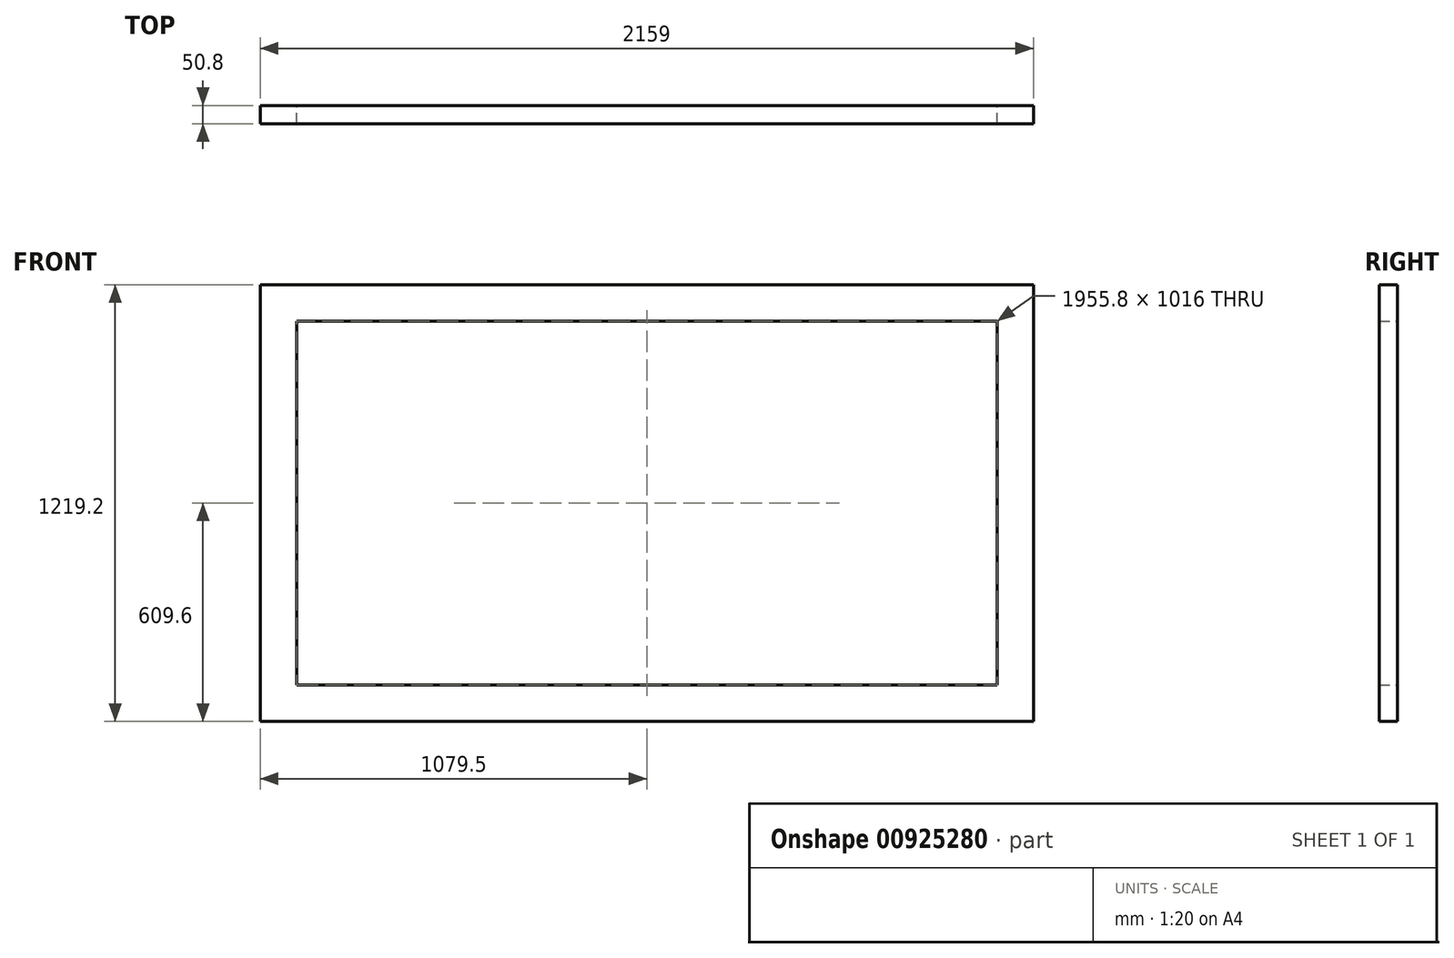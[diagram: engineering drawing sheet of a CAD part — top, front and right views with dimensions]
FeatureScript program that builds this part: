
annotation { "Feature Type Name" : "Feature", "Feature Type Description" : "" }
export const myFeature = defineFeature(function(context is Context, id is Id, definition is map)
    precondition{}
    {
        {
            var Q0;
            Q0=qCreatedBy(makeId("Front.planeOp"),FACE);
            var sketch = newSketch(context, id + "F0", { "sketchPlane" : qUnion([Q0])});
            skLineSegment(sketch, "E0.bottom", {"start": v(0, 0) * mm, "end": v(2159, 0) * mm});
            skLineSegment(sketch, "E0.top", {"start": v(0, 1219.2) * mm, "end": v(2159, 1219.2) * mm});
            skLineSegment(sketch, "E0.left", {"start": v(0, 0) * mm, "end": v(0, 1219.2) * mm});
            skLineSegment(sketch, "E0.right", {"start": v(2159, 0) * mm, "end": v(2159, 1219.2) * mm});
            skLineSegment(sketch, "E1.bottom", {"start": v(101.6, 101.6) * mm, "end": v(2057.4, 101.6) * mm});
            skLineSegment(sketch, "E1.top", {"start": v(101.6, 1117.6) * mm, "end": v(2057.4, 1117.6) * mm});
            skLineSegment(sketch, "E1.left", {"start": v(101.6, 101.6) * mm, "end": v(101.6, 1117.6) * mm});
            skLineSegment(sketch, "E1.right", {"start": v(2057.4, 101.6) * mm, "end": v(2057.4, 1117.6) * mm});
            skSolve(sketch);
        }
        {
            var Q0;
            Q0=makeQuery(id+"F0.imprint","IMPRINT",FACE,{"disambiguationData":[TD([[makeQuery(id+"F0.imprint","IMPRINT",EDGE,{"derivedFrom":sQuery(id+"F0.wireOp",EDGE,"E0.bottom")}),1.0]])]});
            extrude(context, id + "F1", {"entities" : qUnion([Q0]), "depth" : 50.8 * mm, "offsetDistance" : 25.4 * mm});
        }
    });
